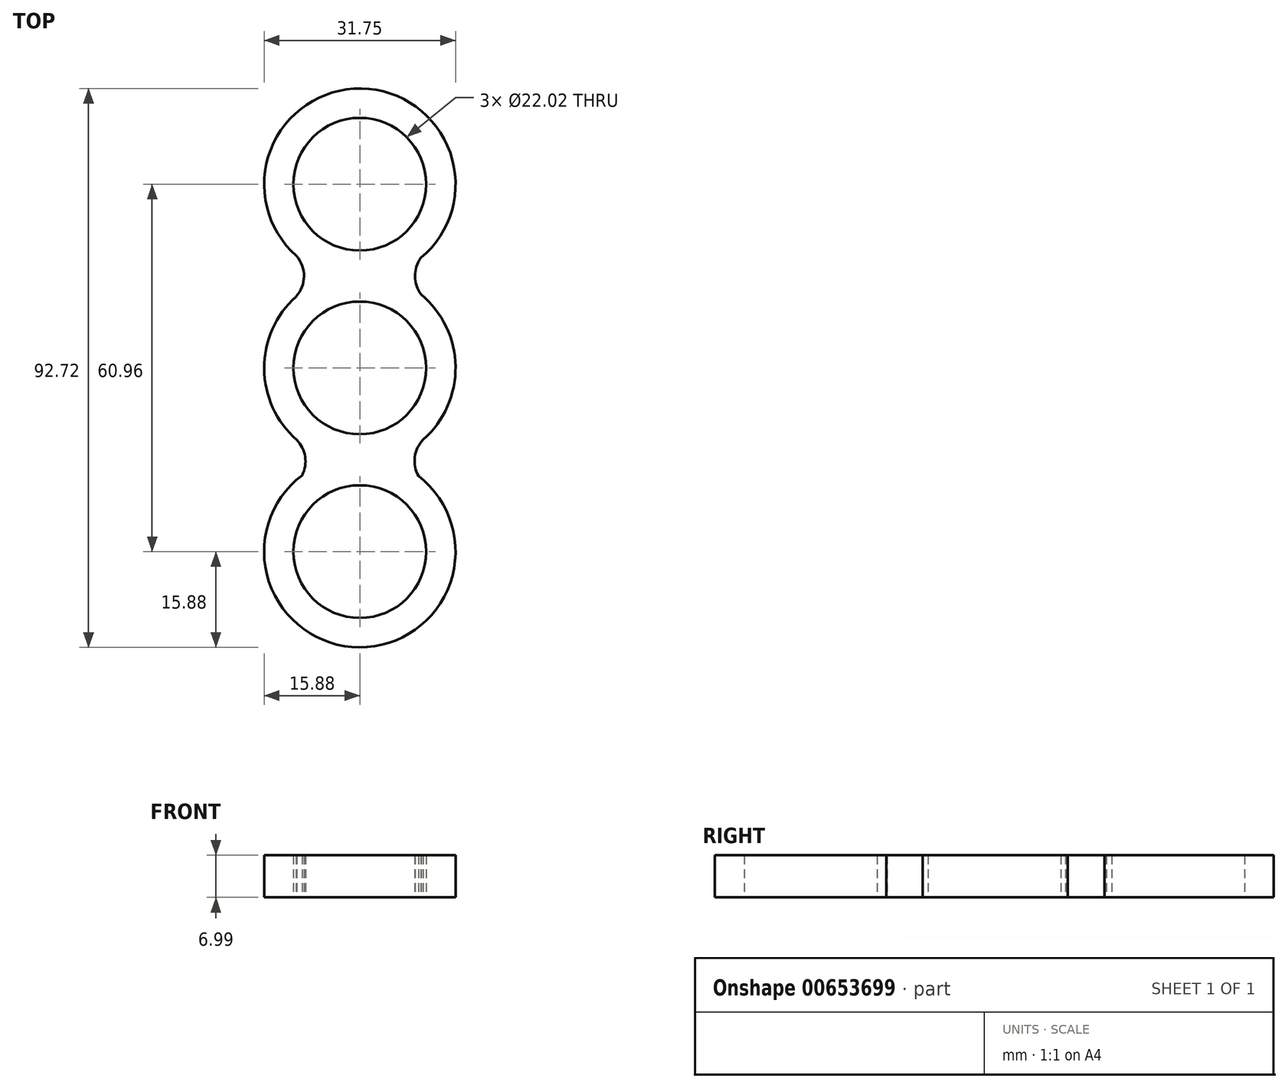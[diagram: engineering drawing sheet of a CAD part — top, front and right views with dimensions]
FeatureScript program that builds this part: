
annotation { "Feature Type Name" : "Feature", "Feature Type Description" : "" }
export const myFeature = defineFeature(function(context is Context, id is Id, definition is map)
    precondition{}
    {
        {
            var Q0;
            Q0=qCreatedBy(makeId("Top.planeOp"),FACE);
            var sketch = newSketch(context, id + "F0", { "sketchPlane" : qUnion([Q0])});
            skCircle(sketch, "E0", {"center": v(0, 0) * mm, "radius": 11.01 * mm});
            skCircle(sketch, "E1", {"center": v(0, 0) * mm, "radius": 15.88 * mm});
            skLineSegment(sketch, "E2", {"start": v(0, 0) * mm, "end": v(0, 30.48) * mm});
            skLineSegment(sketch, "E3", {"start": v(0, 0) * mm, "end": v(0, -30.48) * mm});
            skCircle(sketch, "E4", {"center": v(0, 30.48) * mm, "radius": 15.88 * mm});
            skCircle(sketch, "E5", {"center": v(0, 30.48) * mm, "radius": 11.01 * mm});
            skCircle(sketch, "E6", {"center": v(0, -30.48) * mm, "radius": 15.88 * mm});
            skCircle(sketch, "E7", {"center": v(0, -30.48) * mm, "radius": 11.01 * mm});
            skArc(sketch, "E8", {"start": v(-10.6, 11.81) * mm, "mid": v(-9.28, 15.7) * mm, "end": v(-11.26, 19.29) * mm});
            skArc(sketch, "E9", {"start": v(11.52, 19.55) * mm, "mid": v(9.23, 16.16) * mm, "end": v(10.19, 12.17) * mm});
            skArc(sketch, "E10", {"start": v(-9.58, -17.82) * mm, "mid": v(-9.12, -14.45) * mm, "end": v(-10.9, -11.54) * mm});
            skArc(sketch, "E11", {"start": v(10.93, -11.52) * mm, "mid": v(9.16, -14.51) * mm, "end": v(9.74, -17.94) * mm});
            skSolve(sketch);
        }
        {
            var Q0;
            {var subQ0=sQuery(id+"F0.wireOp",EDGE,"E2");var subQ1=sQuery(id+"F0.wireOp",EDGE,"E1");var subQ2=makeQuery(id+"F0.imprint","INTERSECT",VERTEX,{"derivedFrom":[subQ1,subQ0]});Q0=makeQuery(id+"F0.imprint","IMPRINT",FACE,{"disambiguationData":[TD([[makeQuery(id+"F0.imprint","IMPRINT",EDGE,{"disambiguationData":[TD([[subQ2,1.0]])],"derivedFrom":subQ1}),1.0]])]});}
            var Q1;
            {var subQ0=sQuery(id+"F0.wireOp",EDGE,"E2");var subQ1=sQuery(id+"F0.wireOp",EDGE,"E1");var subQ2=makeQuery(id+"F0.imprint","INTERSECT",VERTEX,{"derivedFrom":[subQ1,subQ0]});Q1=makeQuery(id+"F0.imprint","IMPRINT",FACE,{"disambiguationData":[TD([[makeQuery(id+"F0.imprint","IMPRINT",EDGE,{"disambiguationData":[TD([[subQ2,-1.0]])],"derivedFrom":subQ1}),1.0]])]});}
            var Q2;
            {var subQ0=sQuery(id+"F0.wireOp",EDGE,"E6");var subQ1=sQuery(id+"F0.wireOp",EDGE,"E1");var subQ2=makeQuery(id+"F0.imprint","INTERSECT",VERTEX,{"disambiguationData":[OD(0.0)],"derivedFrom":[subQ1,subQ0]});Q2=makeQuery(id+"F0.imprint","IMPRINT",FACE,{"disambiguationData":[TD([[makeQuery(id+"F0.imprint","IMPRINT",EDGE,{"disambiguationData":[TD([[subQ2,-1.0]])],"derivedFrom":subQ1}),1.0]])]});}
            var Q3;
            {var subQ0=sQuery(id+"F0.wireOp",EDGE,"E3");var subQ1=sQuery(id+"F0.wireOp",EDGE,"E1");var subQ2=makeQuery(id+"F0.imprint","INTERSECT",VERTEX,{"derivedFrom":[subQ1,subQ0]});Q3=makeQuery(id+"F0.imprint","IMPRINT",FACE,{"disambiguationData":[TD([[makeQuery(id+"F0.imprint","IMPRINT",EDGE,{"disambiguationData":[TD([[subQ2,-1.0]])],"derivedFrom":subQ1}),1.0]])]});}
            var Q4;
            {var subQ1=sQuery(id+"F0.wireOp",EDGE,"E0");var subQ5=sQuery(id+"F0.wireOp",EDGE,"E2");var subQ6=makeQuery(id+"F0.imprint","INTERSECT",VERTEX,{"derivedFrom":[subQ1,subQ5]});Q4=makeQuery(id+"F0.imprint","IMPRINT",FACE,{"disambiguationData":[TD([[makeQuery(id+"F0.imprint","IMPRINT",EDGE,{"disambiguationData":[TD([[subQ6,-1.0]])],"derivedFrom":subQ1}),-1.0]])]});}
            var Q5;
            {var subQ0=sQuery(id+"F0.wireOp",EDGE,"E2");var subQ1=sQuery(id+"F0.wireOp",EDGE,"E0");var subQ2=makeQuery(id+"F0.imprint","INTERSECT",VERTEX,{"derivedFrom":[subQ1,subQ0]});Q5=makeQuery(id+"F0.imprint","IMPRINT",FACE,{"disambiguationData":[TD([[makeQuery(id+"F0.imprint","IMPRINT",EDGE,{"disambiguationData":[TD([[subQ2,1.0]])],"derivedFrom":subQ1}),-1.0]])]});}
            var Q6;
            Q6=makeQuery(id+"F0.imprint","IMPRINT",FACE,{"disambiguationData":[TD([[makeQuery(id+"F0.imprint","IMPRINT",EDGE,{"derivedFrom":sQuery(id+"F0.wireOp",EDGE,"E7")}),-1.0]])]});
            var Q7;
            Q7=makeQuery(id+"F0.imprint","IMPRINT",FACE,{"disambiguationData":[TD([[makeQuery(id+"F0.imprint","IMPRINT",EDGE,{"derivedFrom":sQuery(id+"F0.wireOp",EDGE,"E5")}),-1.0]])]});
            extrude(context, id + "F1", {"entities" : qUnion([Q0, Q1, Q2, Q3, Q4, Q5, Q6, Q7]), "depth" : 7 * mm, "offsetDistance" : 25.4 * mm});
        }
        {
            var Q0;
            Q0 = qSketchRegion(id + "F0", true);
            extrude(context, id + "F2", {"entities" : qUnion([Q0]), "operationType" : NewBodyOperationType.ADD, "depth" : 7 * mm, "offsetDistance" : 25.4 * mm});
        }
    });
